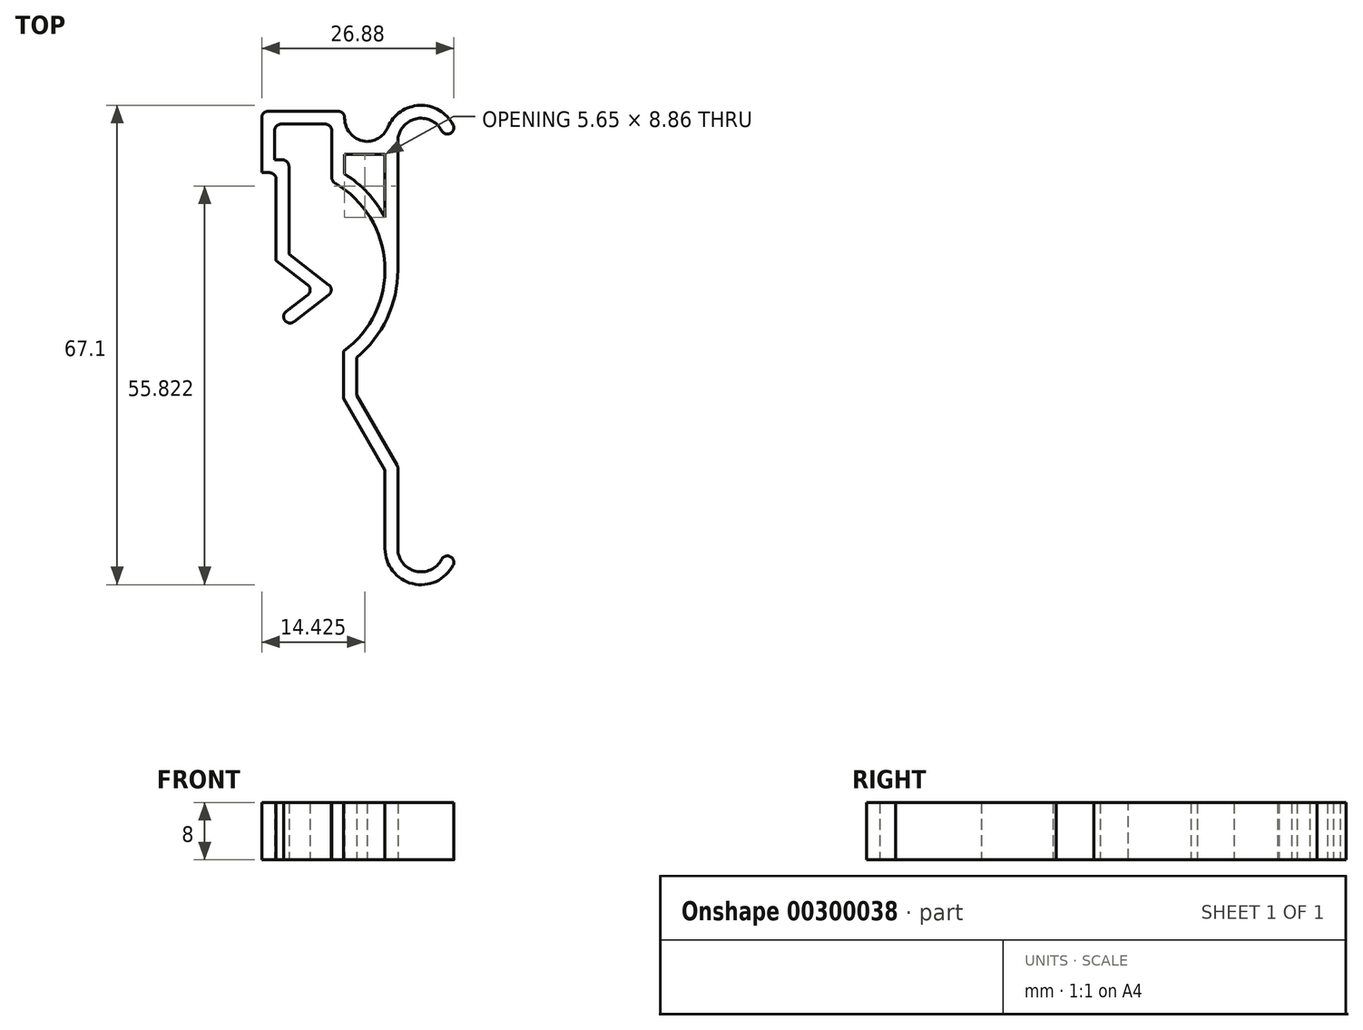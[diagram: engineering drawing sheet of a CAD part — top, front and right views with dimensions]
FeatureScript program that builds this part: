
annotation { "Feature Type Name" : "Feature", "Feature Type Description" : "" }
export const myFeature = defineFeature(function(context is Context, id is Id, definition is map)
    precondition{}
    {
        {
            var Q0;
            Q0=qCreatedBy(makeId("Top.planeOp"),FACE);
            var sketch = newSketch(context, id + "F0", { "sketchPlane" : qUnion([Q0])});
            skLineSegment(sketch, "E0", {"start": v(0, 57) * mm, "end": v(6.5, 57) * mm, "construction": true});
            skArc(sketch, "E1", {"start": v(6.39, 57.84) * mm, "mid": v(2.83, 60.22) * mm, "end": v(0, 57) * mm});
            skLineSegment(sketch, "E2", {"start": v(3.25, 57) * mm, "end": v(6.39, 57.84) * mm, "construction": true});
            skLineSegment(sketch, "E3", {"start": v(0, 28.5) * mm, "end": v(15.36, 28.5) * mm, "construction": true});
            skPoint(sketch, "E3.endSnap0", {"position": v(0, 28.5) * mm});
            skArc(sketch, "E4.MirrorCS", {"start": v(6.39, -0.84) * mm, "mid": v(2.83, -3.22) * mm, "end": v(0, 0) * mm});
            skLineSegment(sketch, "E5", {"start": v(0, 11.5) * mm, "end": v(-5.77, 21.5) * mm});
            skLineSegment(sketch, "E6", {"start": v(-5.77, 21.5) * mm, "end": v(-5.77, 26.75) * mm});
            skLineSegment(sketch, "E7", {"start": v(0, 57) * mm, "end": v(0, 39) * mm});
            skArc(sketch, "E8", {"start": v(0, 39) * mm, "mid": v(-1.52, 32.23) * mm, "end": v(-5.77, 26.75) * mm});
            skLineSegment(sketch, "E9", {"start": v(0, 11.5) * mm, "end": v(0, 0) * mm});
            skArc(sketch, "E10.0", {"start": v(8.13, -1.3) * mm, "mid": v(2.6, -5) * mm, "end": v(-1.8, 0) * mm});
            skLineSegment(sketch, "E10.1", {"start": v(-1.8, 11.02) * mm, "end": v(-1.8, 0) * mm});
            skLineSegment(sketch, "E10.2", {"start": v(-1.8, 11.02) * mm, "end": v(-7.57, 21.02) * mm});
            skArc(sketch, "E10.3", {"start": v(8.13, 58.3) * mm, "mid": v(2.6, 62) * mm, "end": v(-1.8, 57) * mm});
            skLineSegment(sketch, "E10.4", {"start": v(-1.8, 55.2) * mm, "end": v(-1.8, 46.34) * mm});
            skArc(sketch, "E10.5", {"start": v(-1.8, 39) * mm, "mid": v(-3.33, 32.62) * mm, "end": v(-7.57, 27.63) * mm});
            skLineSegment(sketch, "E10.6", {"start": v(-7.57, 21.02) * mm, "end": v(-7.57, 27.63) * mm});
            skLineSegment(sketch, "E11", {"start": v(6.39, 57.84) * mm, "end": v(8.13, 58.3) * mm});
            skLineSegment(sketch, "E12", {"start": v(6.39, -0.84) * mm, "end": v(8.13, -1.3) * mm});
            skArc(sketch, "E13", {"start": v(-1.8, 39) * mm, "mid": v(-3.8, 46.24) * mm, "end": v(-9.25, 51.42) * mm});
            skLineSegment(sketch, "E14", {"start": v(-9.25, 57) * mm, "end": v(-9.25, 51.42) * mm});
            skLineSegment(sketch, "E15.0", {"start": v(-7.45, 55.2) * mm, "end": v(-7.45, 52.46) * mm});
            skArc(sketch, "E16.0", {"start": v(-1.8, 46.34) * mm, "mid": v(-4.22, 49.78) * mm, "end": v(-7.45, 52.46) * mm});
            skLineSegment(sketch, "E17.0", {"start": v(-1.8, 55.2) * mm, "end": v(-7.45, 55.2) * mm});
            skLineSegment(sketch, "E18", {"start": v(-9.25, 51.42) * mm, "end": v(-9.25, 59.42) * mm, "construction": true});
            skLineSegment(sketch, "E19", {"start": v(-9.25, 59.42) * mm, "end": v(-17.25, 59.42) * mm});
            skLineSegment(sketch, "E20", {"start": v(-17.25, 59.42) * mm, "end": v(-17.25, 54.42) * mm});
            skLineSegment(sketch, "E21", {"start": v(-17.25, 54.42) * mm, "end": v(-15.25, 54.42) * mm});
            skLineSegment(sketch, "E22", {"start": v(-15.25, 54.42) * mm, "end": v(-15.25, 41.22) * mm});
            skLineSegment(sketch, "E23", {"start": v(-15.25, 41.22) * mm, "end": v(-8.75, 41.22) * mm, "construction": true});
            skLineSegment(sketch, "E24", {"start": v(-8.75, 41.22) * mm, "end": v(-8.75, 36.22) * mm, "construction": true});
            skLineSegment(sketch, "E25", {"start": v(-15.25, 41.22) * mm, "end": v(-8.75, 36.22) * mm});
            skLineSegment(sketch, "E26", {"start": v(-9.25, 59.42) * mm, "end": v(-9.25, 57) * mm});
            skLineSegment(sketch, "E27", {"start": v(-8.75, 36.22) * mm, "end": v(-8.75, 31.22) * mm, "construction": true});
            skLineSegment(sketch, "E28", {"start": v(-8.75, 31.22) * mm, "end": v(-15.25, 31.22) * mm, "construction": true});
            skLineSegment(sketch, "E29", {"start": v(-15.25, 31.22) * mm, "end": v(-8.75, 36.22) * mm});
            skLineSegment(sketch, "E30.0", {"start": v(-16.35, 32.65) * mm, "end": v(-11.7, 36.22) * mm});
            skLineSegment(sketch, "E30.1", {"start": v(-17.05, 40.34) * mm, "end": v(-11.7, 36.22) * mm});
            skLineSegment(sketch, "E30.2", {"start": v(-17.05, 52.62) * mm, "end": v(-17.05, 40.34) * mm});
            skLineSegment(sketch, "E30.4", {"start": v(-9.7, 61.22) * mm, "end": v(-19.05, 61.22) * mm});
            skLineSegment(sketch, "E30.5", {"start": v(-19.05, 61.22) * mm, "end": v(-19.05, 52.62) * mm});
            skLineSegment(sketch, "E30.6", {"start": v(-19.05, 52.62) * mm, "end": v(-17.05, 52.62) * mm});
            skLineSegment(sketch, "E31", {"start": v(-16.35, 32.65) * mm, "end": v(-15.25, 31.22) * mm});
            skLineSegment(sketch, "E32", {"start": v(-7.45, 57) * mm, "end": v(-7.45, 61.22) * mm});
            skLineSegment(sketch, "E33", {"start": v(-7.45, 61.22) * mm, "end": v(-9.7, 61.22) * mm});
            skLineSegment(sketch, "E34", {"start": v(-7.45, 57) * mm, "end": v(-1.8, 57) * mm});
            skSolve(sketch);
        }
        {
            var Q0;
            Q0=makeQuery(id+"F0.imprint","IMPRINT",FACE,{"disambiguationData":[TD([[makeQuery(id+"F0.imprint","IMPRINT",EDGE,{"derivedFrom":sQuery(id+"F0.wireOp",EDGE,"E1")}),-1.0]])]});
            extrude(context, id + "F1", {"entities" : qUnion([Q0]), "depth" : 8 * mm});
        }
        {
            var Q0;
            Q0=makeQuery(id+"F1.opExtrude","SWEPT_EDGE",EDGE,{"disambiguationData":[OSD([sQuery(id+"F0.wireOp",EDGE,"E10.3"),sQuery(id+"F0.wireOp",EDGE,"E11")])]});
            var Q1;
            Q1=makeQuery(id+"F1.opExtrude","SWEPT_EDGE",EDGE,{"disambiguationData":[OSD([sQuery(id+"F0.wireOp",EDGE,"E1"),sQuery(id+"F0.wireOp",EDGE,"E11")])]});
            var Q2;
            Q2=makeQuery(id+"F1.opExtrude","SWEPT_EDGE",EDGE,{"disambiguationData":[OSD([sQuery(id+"F0.wireOp",EDGE,"E10.0"),sQuery(id+"F0.wireOp",EDGE,"E12")])]});
            var Q3;
            Q3=makeQuery(id+"F1.opExtrude","SWEPT_EDGE",EDGE,{"disambiguationData":[OSD([sQuery(id+"F0.wireOp",EDGE,"E4.MirrorCS"),sQuery(id+"F0.wireOp",EDGE,"E12")])]});
            var Q4;
            Q4=makeQuery(id+"F1.opExtrude","SWEPT_EDGE",EDGE,{"disambiguationData":[OSD([sQuery(id+"F0.wireOp",EDGE,"E30.0"),sQuery(id+"F0.wireOp",EDGE,"E30.1")])]});
            var Q5;
            Q5=makeQuery(id+"F1.opExtrude","SWEPT_EDGE",EDGE,{"disambiguationData":[OSD([sQuery(id+"F0.wireOp",EDGE,"E30.0"),sQuery(id+"F0.wireOp",EDGE,"E31")])]});
            var Q6;
            Q6=makeQuery(id+"F1.opExtrude","SWEPT_EDGE",EDGE,{"disambiguationData":[OSD([sQuery(id+"F0.wireOp",EDGE,"E29"),sQuery(id+"F0.wireOp",EDGE,"E31")])]});
            var Q7;
            Q7=makeQuery(id+"F1.opExtrude","SWEPT_EDGE",EDGE,{"disambiguationData":[OSD([sQuery(id+"F0.wireOp",EDGE,"E25"),sQuery(id+"F0.wireOp",EDGE,"E29")])]});
            var Q8;
            Q8=makeQuery(id+"F1.opExtrude","SWEPT_EDGE",EDGE,{"disambiguationData":[OSD([sQuery(id+"F0.wireOp",EDGE,"E19"),sQuery(id+"F0.wireOp",EDGE,"E20")])]});
            var Q9;
            Q9=makeQuery(id+"F1.opExtrude","SWEPT_EDGE",EDGE,{"disambiguationData":[OSD([sQuery(id+"F0.wireOp",EDGE,"E21"),sQuery(id+"F0.wireOp",EDGE,"E22")])]});
            var Q10;
            Q10=makeQuery(id+"F1.opExtrude","SWEPT_EDGE",EDGE,{"disambiguationData":[OSD([sQuery(id+"F0.wireOp",EDGE,"E19"),sQuery(id+"F0.wireOp",EDGE,"E26")])]});
            var Q11;
            Q11=makeQuery(id+"F1.opExtrude","SWEPT_EDGE",EDGE,{"disambiguationData":[OSD([sQuery(id+"F0.wireOp",EDGE,"E30.4"),sQuery(id+"F0.wireOp",EDGE,"E30.5")])]});
            var Q12;
            Q12=makeQuery(id+"F1.opExtrude","SWEPT_EDGE",EDGE,{"disambiguationData":[OSD([sQuery(id+"F0.wireOp",EDGE,"E30.2"),sQuery(id+"F0.wireOp",EDGE,"E30.6")])]});
            var Q13;
            Q13=makeQuery(id+"F1.opExtrude","SWEPT_EDGE",EDGE,{"disambiguationData":[OSD([sQuery(id+"F0.wireOp",EDGE,"E13"),sQuery(id+"F0.wireOp",EDGE,"E14")])]});
            var Q14;
            Q14=makeQuery(id+"F1.opExtrude","SWEPT_EDGE",EDGE,{"disambiguationData":[OSD([sQuery(id+"F0.wireOp",EDGE,"E30.4"),sQuery(id+"F0.wireOp",EDGE,"293160bd-5398-4315-b450-ddf07c9ad3f8.trimOffspring")])]});
            var Q15;
            Q15=makeQuery(id+"F1.opExtrude","SWEPT_EDGE",EDGE,{"disambiguationData":[OSD([sQuery(id+"F0.wireOp",EDGE,"E5"),sQuery(id+"F0.wireOp",EDGE,"E9")])]});
            var Q16;
            Q16=makeQuery(id+"F1.opExtrude","SWEPT_EDGE",EDGE,{"disambiguationData":[OSD([sQuery(id+"F0.wireOp",EDGE,"E32"),sQuery(id+"F0.wireOp",EDGE,"E33")])]});
            fillet(context, id + "F2", {"entities" : qUnion([Q0, Q1, Q2, Q3, Q4, Q5, Q6, Q7, Q8, Q9, Q10, Q11, Q12, Q13, Q14, Q15, Q16]), "radius" : .9 * mm, "tangentPropagation" : true, "allowEdgeOverflow" : false});
        }
        {
            var Q0;
            Q0=makeQuery(id+"F1.opExtrude","SWEPT_EDGE",EDGE,{"disambiguationData":[OSD([sQuery(id+"F0.wireOp",EDGE,"E10.3"),sQuery(id+"F0.wireOp",EDGE,"zvmEg1RP-bzG7-VyuS-xTAE-JL4nivRw8E9J")])]});
            var Q1;
            Q1=makeQuery(id+"F1.opExtrude","SWEPT_EDGE",EDGE,{"disambiguationData":[OSD([sQuery(id+"F0.wireOp",EDGE,"zvmEg1RP-bzG7-VyuS-xTAE-JL4nivRw8E9J"),sQuery(id+"F0.wireOp",EDGE,"293160bd-5398-4315-b450-ddf07c9ad3f8.trimOffspring")])]});
            var Q2;
            Q2=makeQuery(id+"F1.opExtrude","SWEPT_EDGE",EDGE,{"disambiguationData":[OSD([sQuery(id+"F0.wireOp",EDGE,"E32"),sQuery(id+"F0.wireOp",EDGE,"E34")])]});
            fillet(context, id + "F3", {"entities" : qUnion([Q0, Q1, Q2]), "radius" : 3.25 * mm, "tangentPropagation" : true, "allowEdgeOverflow" : false});
        }
    });
